# Revit family: IS_Connect_E7718_BIM_FR
name_source: partatom
category: Plumbing Fixtures
revit_build: Autodesk Revit 2017 (Build: 20160225_1515(x64)
units: mm (PartAtom-declared; Revit-internal decimal feet)

## family parameters
Always vertical = No
Cut with Voids When Loaded = No
OmniClass Number = 23.45.05.21.11.11
OmniClass Title = Water Operated Water Closets
Part Type = Normal
Room Calculation Point = No
Round Connector Dimension = Use Diameter
Shared = No
Work Plane-Based = No

## types (2) — shared parameters
Accessoires = www.idealstandard.be
Auteur = Ideal Standard
BOSUseNativeGeometries = 1
ConseilsDInstallation = www.idealstandard.be
DateDeCréation = 2018_08_15
Dimensions = 348 x 540 x 362mm
Espace = Interne
Forme = Sculptured
Hauteur = 348 mm  [stored 1.14173 ft]
IfcExportAs = IfcSanitaryTerminalType
IfcExportType = TOILETPANS
InformationsProduit = www.idealstandard.be
Largeur = 362 mm  [stored 1.18766 ft]
LienUtile = www.idealstandard.be
Longueur = 540 mm  [stored 1.77165 ft]
Manufacturer = www.idealstandard.be
Marque = Ideal Standard
NominalHeight = 348 mm  [stored 1.14173 ft]
NominalLength = 540 mm  [stored 1.77165 ft]
NominalWidth = 362 mm  [stored 1.18766 ft]
PerformanceDeDurabilité = 25
PoidsNet = 24
Profondeur = 540 mm  [stored 1.77165 ft]
Raccordement = plomberie
Révision = 1
Size = 348 x 540 x 362mm
URL = www.idealstandard.be
Uniclass2015Code = Pr_40_20_93_94
Uniclass2015Title = WC pans
Uniclass2015Version = Products v1.1
UnitéDeMesure = millimètres
UnitéDeTemps = an
UnitéMonétaire = €
UrlDuFabricant = www.idealstandard.be
Version = 1
zero-valued in all types: Cost, CoûtDeRemplacement

## per-type parameters (varying)
| type | Bim-NomDuProjet | CodeBarre | Couleur | Description | Finition | Model | Nom | Référence |
| E771801 - CONNECT wall mounted bowl 360x540mm, wash-down | ISI_IdealStandard_WcPans_Connect_E771801 | 5017830474746 | White | CONNECT CUVETTE SUSPENDUE,  360x540mm, LAVAGE VERS LE BAS, BLANC | White | E771801 | WcPans_Connect_E771801_IdealStandard | E771801 |
| E7718MA - CONNECT wall mounted bowl 360x540mm, wash-down | ISI_IdealStandard_WcPans_Connect_E7718MA | 5017830484370 | WHITE IP | Connect - Cuvette suspendue | WHITE IP | E7718MA | WcPans_Connect_E7718MA_IdealStandard | E7718MA |

note: [stored X ft] marks values corroborated as IEEE doubles in the binary element streams (Revit-internal decimal feet)

## geometry (parser evidence)
native form markers: Sweep x2
no freeform markers — native parametric forms only
